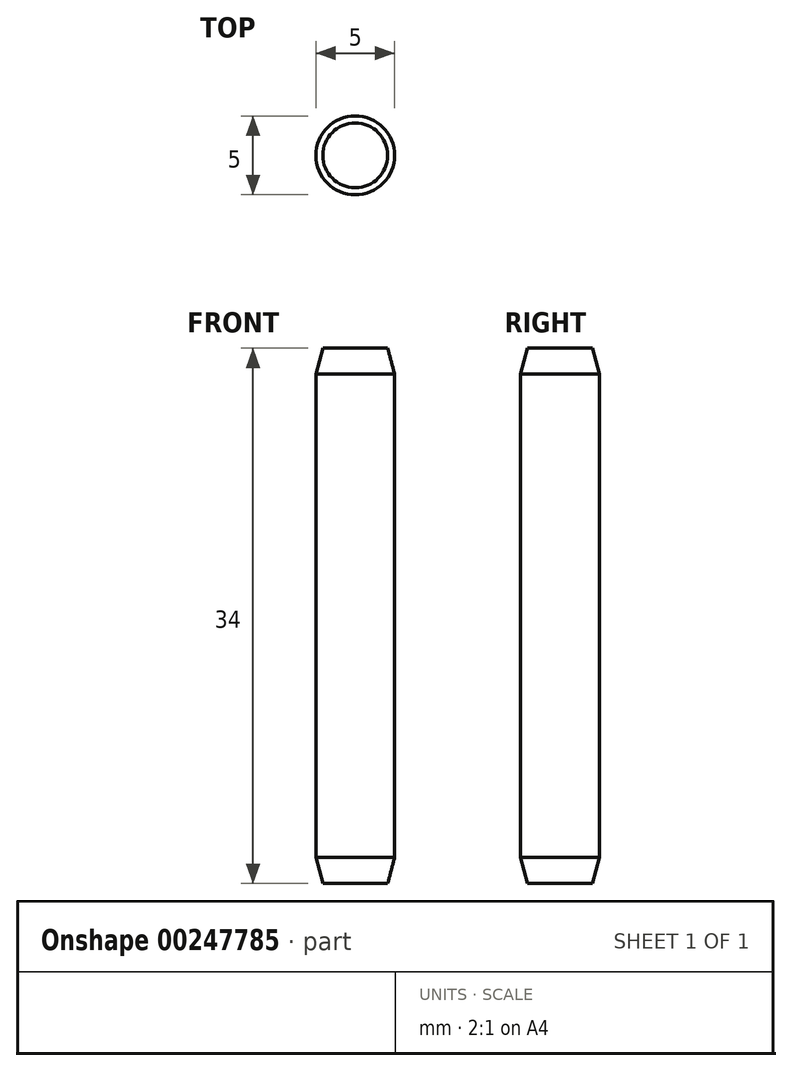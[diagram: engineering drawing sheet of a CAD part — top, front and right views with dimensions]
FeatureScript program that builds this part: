
annotation { "Feature Type Name" : "Feature", "Feature Type Description" : "" }
export const myFeature = defineFeature(function(context is Context, id is Id, definition is map)
    precondition{}
    {
        {
            var Q0;
            Q0=qCreatedBy(makeId("Front.planeOp"),FACE);
            var sketch = newSketch(context, id + "F0", { "sketchPlane" : qUnion([Q0])});
            skLineSegment(sketch, "E0", {"start": v(-2.06, 17) * mm, "end": v(-2.5, 15.36) * mm});
            skLineSegment(sketch, "E1", {"start": v(-2.5, 15.36) * mm, "end": v(-2.5, -15.36) * mm});
            skLineSegment(sketch, "E2.MirrorCS", {"start": v(-2.06, -17) * mm, "end": v(-2.5, -15.36) * mm});
            skPoint(sketch, "E3.orphan", {"position": v(-2.5, 0) * mm});
            skLineSegment(sketch, "E4", {"start": v(-2.06, 17) * mm, "end": v(0, 17) * mm});
            skLineSegment(sketch, "E5", {"start": v(-2.06, -17) * mm, "end": v(0, -17) * mm});
            skLineSegment(sketch, "E6", {"start": v(0, 17) * mm, "end": v(0, -17) * mm});
            skSolve(sketch);
        }
        {
            var Q0;
            Q0=qSketchRegion(id+"F0",true);
            var Q1;
            Q1=sQuery(id+"F0.wireOp",EDGE,"E6");
            revolve(context, id + "F1", {"entities" : qUnion([Q0]), "axis" : qUnion([Q1]), "revolveType" : RevolveType.FULL});
        }
    });
